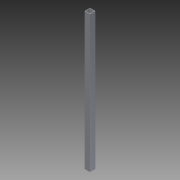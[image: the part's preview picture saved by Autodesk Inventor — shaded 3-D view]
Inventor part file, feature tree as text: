
AUTODESK INVENTOR PART (.ipt)
format: ipt  version: 2013 (Build 170138000, 138)  size: 74,752 bytes
history: native  units: in
note: dims shown in document units (in); Inventor stores cm internally (conversion verified against a paired STEP export)
features: extrude x1, sketch x1
ambient origin geometry x8: Origin, YZ Plane, XZ Plane, XY Plane, X Axis, Y Axis, Z Axis, Center Point
bodies: Solid1 (feature_tree)
feature tree (2):
  extrude  "Extrusion1"  Depth=1.0in
  sketch  "Sketch1"  dims[d0=1.0in d2=1.0in d3=0.0625in d4=23.375in d5=0.0in]
